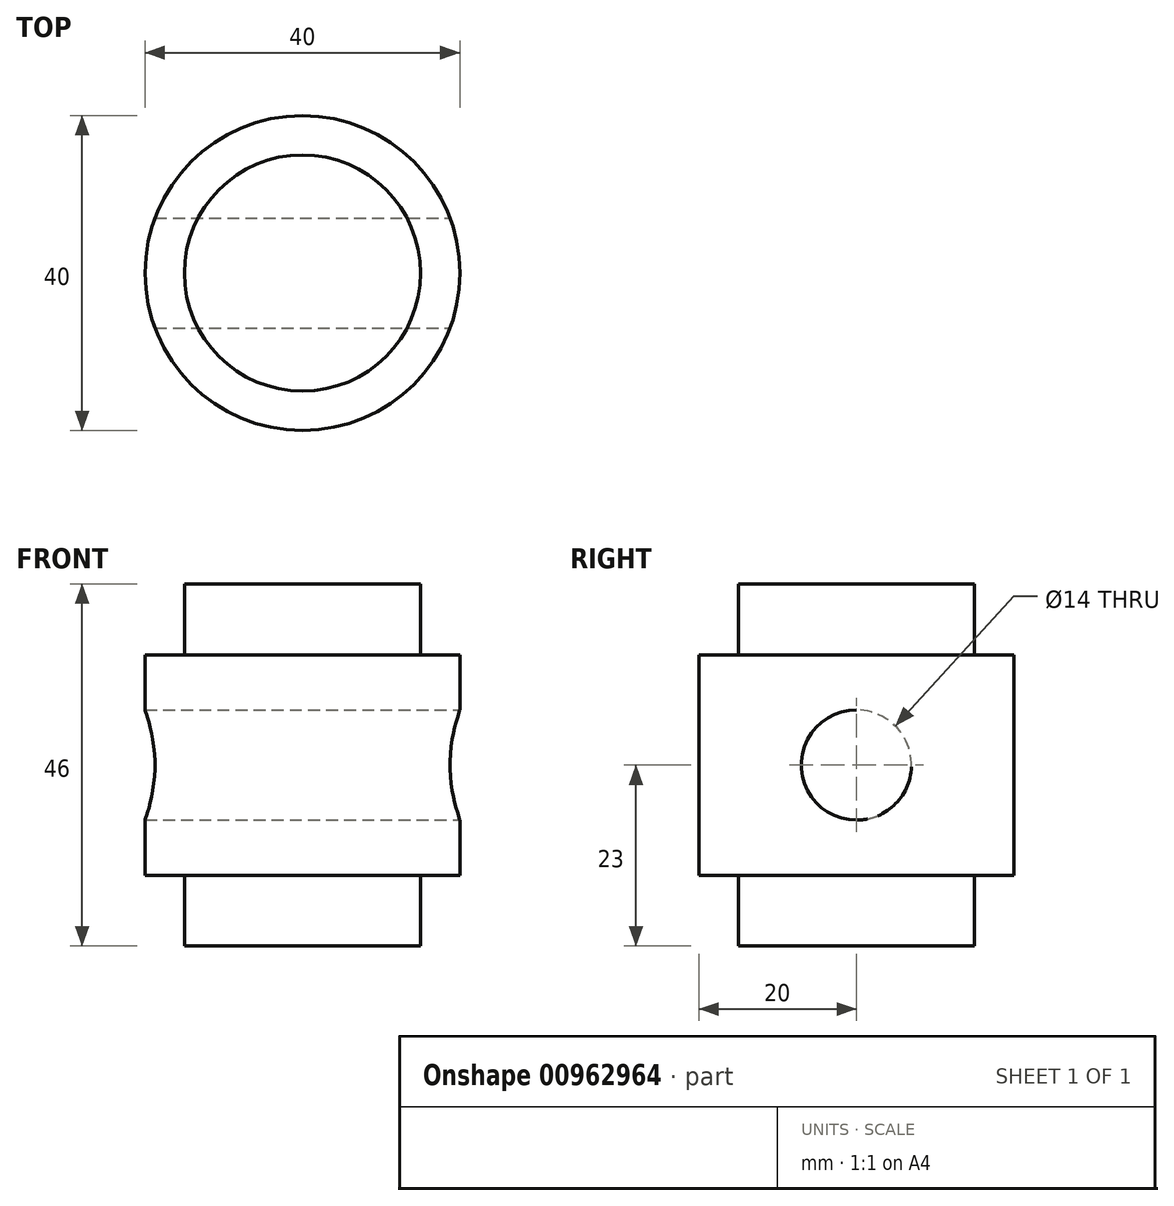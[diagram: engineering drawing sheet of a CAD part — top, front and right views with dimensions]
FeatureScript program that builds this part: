
annotation { "Feature Type Name" : "Feature", "Feature Type Description" : "" }
export const myFeature = defineFeature(function(context is Context, id is Id, definition is map)
    precondition{}
    {
        {
            var Q0;
            Q0=qCreatedBy(makeId("Top.planeOp"),FACE);
            var sketch = newSketch(context, id + "F0", { "sketchPlane" : qUnion([Q0])});
            skCircle(sketch, "E0", {"center": v(0, 0) * mm, "radius": 15 * mm});
            skSolve(sketch);
        }
        {
            var Q0;
            Q0 = qSketchRegion(id + "F0", true);
            extrude(context, id + "F1", {"entities" : qUnion([Q0]), "depth" : 36 * mm, "offsetDistance" : 25 * mm, "symmetric" : true});
        }
        {
            var Q0;
            Q0=makeQuery(id+"F1.opExtrude","CAP_FACE",FACE,{"disambiguationData":[OSD([sQuery(id+"F0.wireOp",EDGE,"E0")])],"isStart":false});
            var sketch = newSketch(context, id + "F2", { "sketchPlane" : qUnion([Q0])});
            skCircle(sketch, "E1", {"center": v(0, 0) * mm, "radius": 15 * mm});
            skSolve(sketch);
        }
        {
            var Q0;
            Q0 = qSketchRegion(id + "F2", true);
            extrude(context, id + "F3", {"entities" : qUnion([Q0]), "operationType" : NewBodyOperationType.ADD, "depth" : 5 * mm, "offsetDistance" : 25 * mm});
        }
        {
            var Q0;
            Q0=makeQuery(id+"F1.opExtrude","CAP_FACE",FACE,{"disambiguationData":[OSD([sQuery(id+"F0.wireOp",EDGE,"E0")])],"isStart":true});
            var sketch = newSketch(context, id + "F4", { "sketchPlane" : qUnion([Q0])});
            skCircle(sketch, "E2", {"center": v(0, 0) * mm, "radius": 15 * mm});
            skSolve(sketch);
        }
        {
            var Q0;
            Q0 = qSketchRegion(id + "F4", true);
            extrude(context, id + "F5", {"entities" : qUnion([Q0]), "operationType" : NewBodyOperationType.ADD, "depth" : 5 * mm, "offsetDistance" : 25 * mm});
        }
        {
            var Q0;
            Q0=qCreatedBy(makeId("Right.planeOp"),FACE);
            var sketch = newSketch(context, id + "F6", { "sketchPlane" : qUnion([Q0])});
            skCircle(sketch, "E3", {"center": v(0, 0) * mm, "radius": 7 * mm});
            skSolve(sketch);
        }
        {
            var Q0;
            Q0=qCreatedBy(makeId("Top.planeOp"),FACE);
            var sketch = newSketch(context, id + "F7", { "sketchPlane" : qUnion([Q0])});
            skCircle(sketch, "E4", {"center": v(0, 0) * mm, "radius": 20 * mm});
            skSolve(sketch);
        }
        {
            var Q0;
            Q0 = qSketchRegion(id + "F7", true);
            extrude(context, id + "F8", {"entities" : qUnion([Q0]), "operationType" : NewBodyOperationType.ADD, "depth" : 14 * mm, "offsetDistance" : 25 * mm, "hasSecondDirection" : true, "secondDirectionOppositeDirection" : true, "secondDirectionDepth" : 14 * mm});
        }
        {
            var Q0;
            Q0 = qSketchRegion(id + "F6", true);
            extrude(context, id + "F9", {"entities" : qUnion([Q0]), "operationType" : NewBodyOperationType.REMOVE, "endBound" : BoundingType.THROUGH_ALL, "oppositeDirection" : true, "depth" : 25 * mm, "offsetDistance" : 25 * mm, "hasSecondDirection" : true, "secondDirectionBound" : BoundingType.THROUGH_ALL, "secondDirectionOppositeDirection" : false, "secondDirectionDepth" : 25 * mm});
        }
    });
